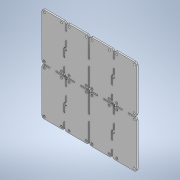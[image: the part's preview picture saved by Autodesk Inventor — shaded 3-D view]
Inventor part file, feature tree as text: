
AUTODESK INVENTOR PART (.ipt)
format: ipt  version: 2021 (Build 250183000, 183)  size: 412,160 bytes
history: native  units: mm
features: extrude x3, sketch x3, fillet x2, other x1, hole x1, pattern_linear x1
ambient origin geometry x8: Origin, YZ Plane, XZ Plane, XY Plane, X Axis, Y Axis, Z Axis, Center Point
bodies: Body1 (feature_tree)
feature tree (11):
  other  "ソリッド1"
  extrude  "押し出し1"  Depth=49.5mm
  extrude  "押し出し2"  Depth=49.5mm
  hole  "穴1"  [1 undecoded]
  pattern_linear  "矩形状パターン1"  Spacing1=1.6mm  [1 undecoded]
  extrude  "押し出し5"  Depth=50.5mm
  fillet  "フィレット3"  Radius=2.5mm
  fillet  "フィレット4"  Radius=2.5mm
  sketch  "スケッチ1"
  sketch  "スケッチ3"
  sketch  "スケッチ7"
note: 2 required parameter values undecoded (feature->parameter linkage not recoverable at this tier; creation-order binding heuristic only, values carry confidence <= 0.55)
